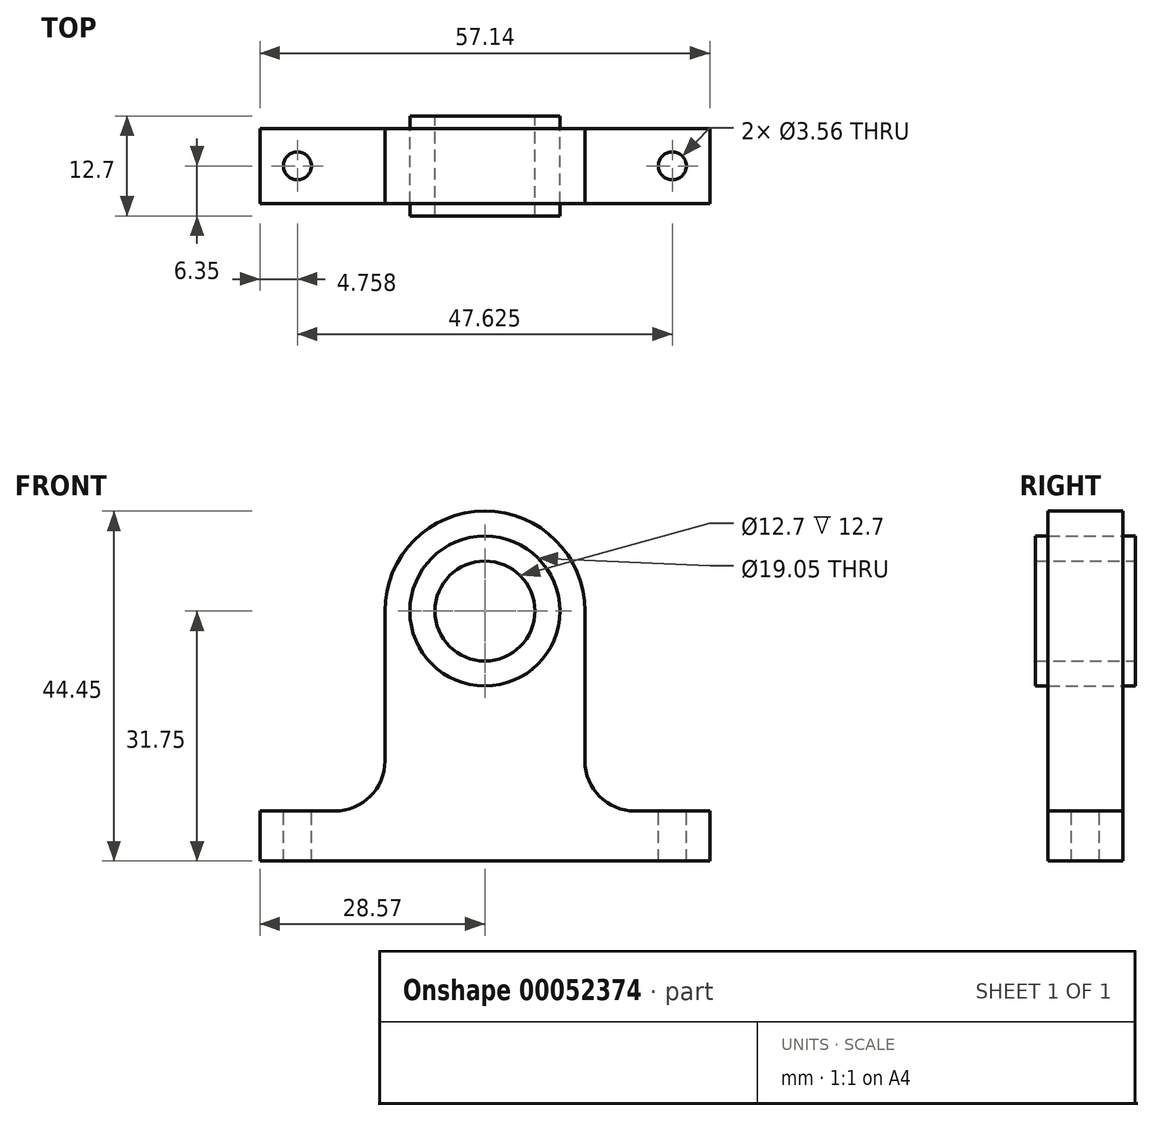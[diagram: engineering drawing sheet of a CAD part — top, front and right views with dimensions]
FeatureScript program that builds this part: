
annotation { "Feature Type Name" : "Feature", "Feature Type Description" : "" }
export const myFeature = defineFeature(function(context is Context, id is Id, definition is map)
    precondition{}
    {
        {
            var Q0;
            Q0=qCreatedBy(makeId("Front.planeOp"),FACE);
            var sketch = newSketch(context, id + "F0", { "sketchPlane" : qUnion([Q0])});
            skArc(sketch, "E0", {"start": v(-12.7, 0) * mm, "mid": v(0, 12.7) * mm, "end": v(12.7, 0) * mm});
            skLineSegment(sketch, "E1", {"start": v(-12.7, 0) * mm, "end": v(-12.7, -19.05) * mm});
            skLineSegment(sketch, "E2", {"start": v(-19.05, -25.4) * mm, "end": v(-28.58, -25.4) * mm});
            skLineSegment(sketch, "E3", {"start": v(-28.58, -25.4) * mm, "end": v(-28.58, -31.75) * mm});
            skLineSegment(sketch, "E4", {"start": v(-28.58, -31.75) * mm, "end": v(28.58, -31.75) * mm});
            skLineSegment(sketch, "E5", {"start": v(28.57, -31.75) * mm, "end": v(28.57, -25.4) * mm});
            skLineSegment(sketch, "E6", {"start": v(28.58, -25.4) * mm, "end": v(19.05, -25.4) * mm});
            skLineSegment(sketch, "E7", {"start": v(12.7, -19.05) * mm, "end": v(12.7, 0) * mm});
            skCircle(sketch, "E8", {"center": v(0, 0) * mm, "radius": 9.53 * mm});
            skPoint(sketch, "E9", {"position": v(0, -31.75) * mm});
            skPoint(sketch, "E10.visualSharp", {"position": v(-12.7, -25.4) * mm});
            skArc(sketch, "E10.filletArc", {"start": v(-19.05, -25.4) * mm, "mid": v(-14.56, -23.54) * mm, "end": v(-12.7, -19.05) * mm});
            skPoint(sketch, "E11.visualSharp", {"position": v(12.7, -25.4) * mm});
            skArc(sketch, "E11.filletArc", {"start": v(12.7, -19.05) * mm, "mid": v(14.56, -23.54) * mm, "end": v(19.05, -25.4) * mm});
            skSolve(sketch);
        }
        {
            var Q0;
            Q0 = qSketchRegion(id + "F0", true);
            extrude(context, id + "F1", {"entities" : qUnion([Q0]), "depth" : 9.52 * mm, "symmetric" : true});
        }
        {
            var Q0;
            Q0=makeQuery(id+"F1.opExtrude","SWEPT_FACE",FACE,{"disambiguationData":[OSD([sQuery(id+"F0.wireOp",EDGE,"E4")])]});
            var sketch = newSketch(context, id + "F2", { "sketchPlane" : qUnion([Q0])});
            skPoint(sketch, "E12", {"position": v(23.81, 0) * mm});
            skPoint(sketch, "E13", {"position": v(-23.81, 0) * mm});
            skSolve(sketch);
        }
        {
            var Q0;
            Q0=sQuery(id+"F2.wireOp",VERTEX,"E13");
            var Q1;
            Q1=sQuery(id+"F2.wireOp",VERTEX,"E12");
            var Q2;
            Q2=makeQuery(id+"F1.opExtrude","SWEPT_BODY",BODY,{"disambiguationData":[OSD([sQuery(id+"F0.wireOp",EDGE,"E0"),sQuery(id+"F0.wireOp",EDGE,"E1"),sQuery(id+"F0.wireOp",EDGE,"E2"),sQuery(id+"F0.wireOp",EDGE,"E3"),sQuery(id+"F0.wireOp",EDGE,"E4"),sQuery(id+"F0.wireOp",EDGE,"E5"),sQuery(id+"F0.wireOp",EDGE,"E6"),sQuery(id+"F0.wireOp",EDGE,"E7"),sQuery(id+"F0.wireOp",EDGE,"E8"),sQuery(id+"F0.wireOp",EDGE,"E10.filletArc"),sQuery(id+"F0.wireOp",EDGE,"E11.filletArc")])]});
            hole(context, id + "F3", {"style" : HoleStyle.SIMPLE, "holeDiameter" : 3.56 * mm, "endStyle" : HoleEndStyle.THROUGH, "locations" : qUnion([Q0, Q1]), "scope" : qUnion([Q2])});
        }
        {
            var Q0;
            Q0=qCreatedBy(makeId("Front.planeOp"),FACE);
            var sketch = newSketch(context, id + "F4", { "sketchPlane" : qUnion([Q0])});
            skCircle(sketch, "E14", {"center": v(0, 0) * mm, "radius": 9.53 * mm});
            skCircle(sketch, "E15", {"center": v(0, 0) * mm, "radius": 6.35 * mm});
            skSolve(sketch);
        }
        {
            var Q0;
            Q0 = qSketchRegion(id + "F4", true);
            extrude(context, id + "F5", {"entities" : qUnion([Q0]), "depth" : 12.7 * mm, "symmetric" : true});
        }
    });
